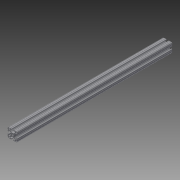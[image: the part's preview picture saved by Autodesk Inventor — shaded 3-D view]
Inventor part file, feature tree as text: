
AUTODESK INVENTOR PART (.ipt)
format: ipt  version: 2013 (Build 170138000, 138)  size: 289,792 bytes
history: native  units: in
note: dims shown in document units (in); Inventor stores cm internally (conversion verified against a paired STEP export)
features: extrude x1, sketch x1
ambient origin geometry x8: Origin, YZ Plane, XZ Plane, XY Plane, X Axis, Y Axis, Z Axis, Center Point
bodies: Solid1 (feature_tree)
feature tree (2):
  extrude  "Extrusion1"  [1 undecoded]
  sketch  "Sketch1"  dims[d0=25.0in d1=0.0in]
note: 1 required parameter value undecoded (feature->parameter linkage not recoverable at this tier; creation-order binding heuristic only, values carry confidence <= 0.55)
